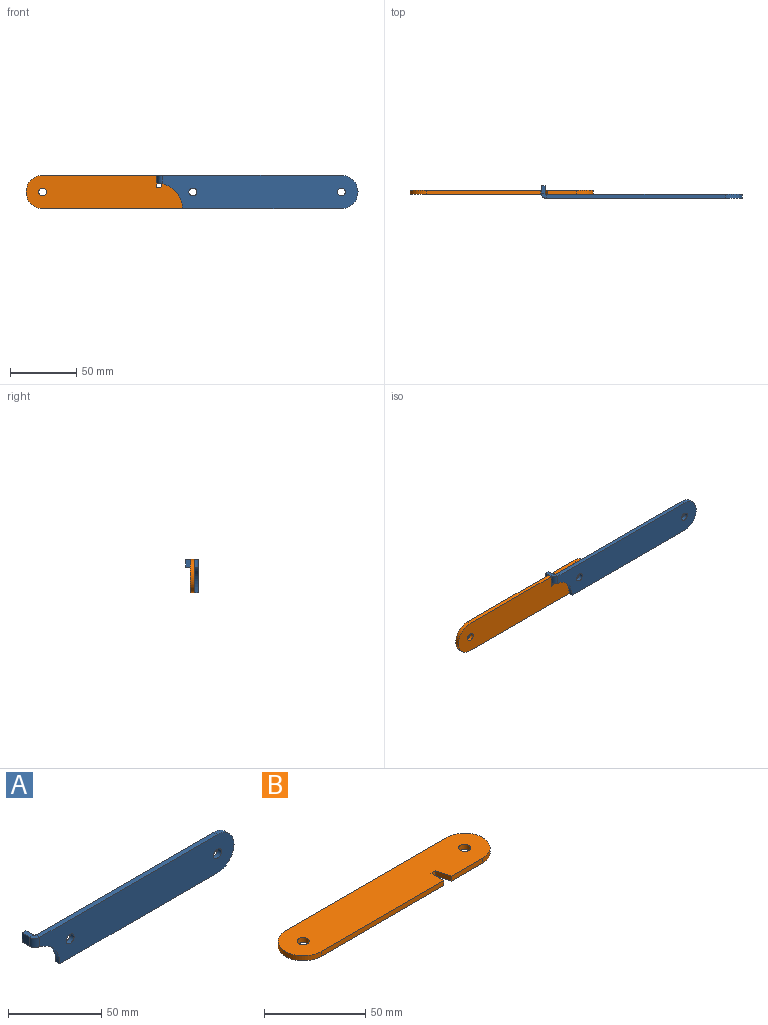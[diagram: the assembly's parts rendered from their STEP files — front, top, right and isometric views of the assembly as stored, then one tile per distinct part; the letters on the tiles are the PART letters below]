
ASSEMBLY  parts=2 mates=1
PART A: 19 faces, bbox 151x9.6x25 mm
  f0: plane 1x0.13mm, normal (0,0,1), area 0mm2, adj f1,f8,f17
  f1: plane 3x0.24mm, normal (-1,0,0), area 0.7mm2, adj f0,f6,f7,f8,f10
  f2: plane 134.5x3mm, normal (0,0,1), area 403.5mm2, adj f7,f8,f9,f16
  f3: plane 119.5x3mm, normal (0,0,-1), area 358.5mm2, adj f6,f7,f8,f9
  f4: cylinder r=3mm len=6mm, axis (0,1,0), area 56.5mm2, adj f7,f8
  f5: cylinder r=3mm len=6mm, axis (0,1,0), area 56.5mm2, adj f7,f8
  f6: cylinder r=19mm len=18.76mm, axis (0,1,0), area 80.5mm2, adj f1,f3,f7,f8
  f7: plane 148x25mm, normal (0,1,0), area 3343.6mm2, adj f1,f2,f3,f4,f5,f6,f9,f10
  f8: plane 148x25mm, normal (0,-1,0), area 3343.6mm2, adj f0,f1,f2,f3,f4,f5,f6,f9
  f9: cylinder r=12.5mm len=25mm, axis (0,1,0), area 117.8mm2, adj f2,f3,f7,f8
  f10: plane 4x3.87mm, normal (0,0,-1), area 8.8mm2, adj f1,f7,f13,f17,f18
  f11: plane 6x3mm, normal (0,1,0), area 18mm2, adj f12,f13,f14,f15
  f12: plane 5.61x3mm, normal (0,0,1), area 16.8mm2, adj f11,f14,f15,f16
  f13: plane 5.61x3mm, normal (0,0,-1), area 16.8mm2, adj f10,f11,f14,f15
  f14: plane 6x5.61mm, normal (1,0,0), area 33.7mm2, adj f11,f12,f13,f18
  f15: plane 6x5.61mm, normal (-1,0,0), area 33.7mm2, adj f11,f12,f13,f17
  f16: plane 4x4mm, normal (0,0,1), area 11.8mm2, adj f2,f12,f17,f18
  f17: cylinder r=4mm len=6mm, axis (0,0,1), area 37.7mm2, adj f0,f8,f10,f15,f16
  f18: cylinder r=1mm len=6mm, axis (0,0,1), area 9.4mm2, adj f7,f10,f14,f16
PART B: 12 faces, bbox 138x25x3 mm
  f0: plane 85.85x3mm, normal (0,-1,0), area 257.6mm2, adj f1,f2,f5,f11
  f1: plane 138x25mm, normal (0,0,-1), area 3221.6mm2, adj f0,f3,f4,f5,f6,f7,f8,f9
  f2: plane 138x25mm, normal (0,0,1), area 3221.6mm2, adj f0,f3,f4,f5,f6,f7,f8,f9
  f3: plane 21.84x3mm, normal (0,-1,0), area 65.5mm2, adj f1,f2,f6,f9
  f4: plane 113x3mm, normal (0,1,0), area 339mm2, adj f1,f2,f5,f6
  f5: cylinder r=12.5mm len=25mm, axis (0,0,1), area 117.8mm2, adj f0,f1,f2,f4
  f6: cylinder r=12.5mm len=25mm, axis (0,0,-1), area 117.8mm2, adj f1,f2,f3,f4
  f7: cylinder r=3mm len=6mm, axis (0,0,1), area 56.5mm2, adj f1,f2
  f8: cylinder r=3mm len=6mm, axis (0,0,1), area 56.5mm2, adj f1,f2
  f9: plane 9x3mm, normal (-0.97,-0.24,0), area 27.8mm2, adj f1,f2,f3,f10
  f10: plane 3.07x3mm, normal (0,-1,0), area 9.2mm2, adj f1,f2,f9,f11
  f11: plane 9x3mm, normal (1,0,0), area 27mm2, adj f0,f1,f2,f10
PLACE A t=(-3.03,-35.74,-79.02)mm
PLACE B rot(axis=(-1,0,0),90deg) t=(-108.58,-35.74,-79.02)mm
MATE revolute A.f5 <-> B.f6  axis (0,1,0) through (-50.06,-35.74,-66.52)mm
